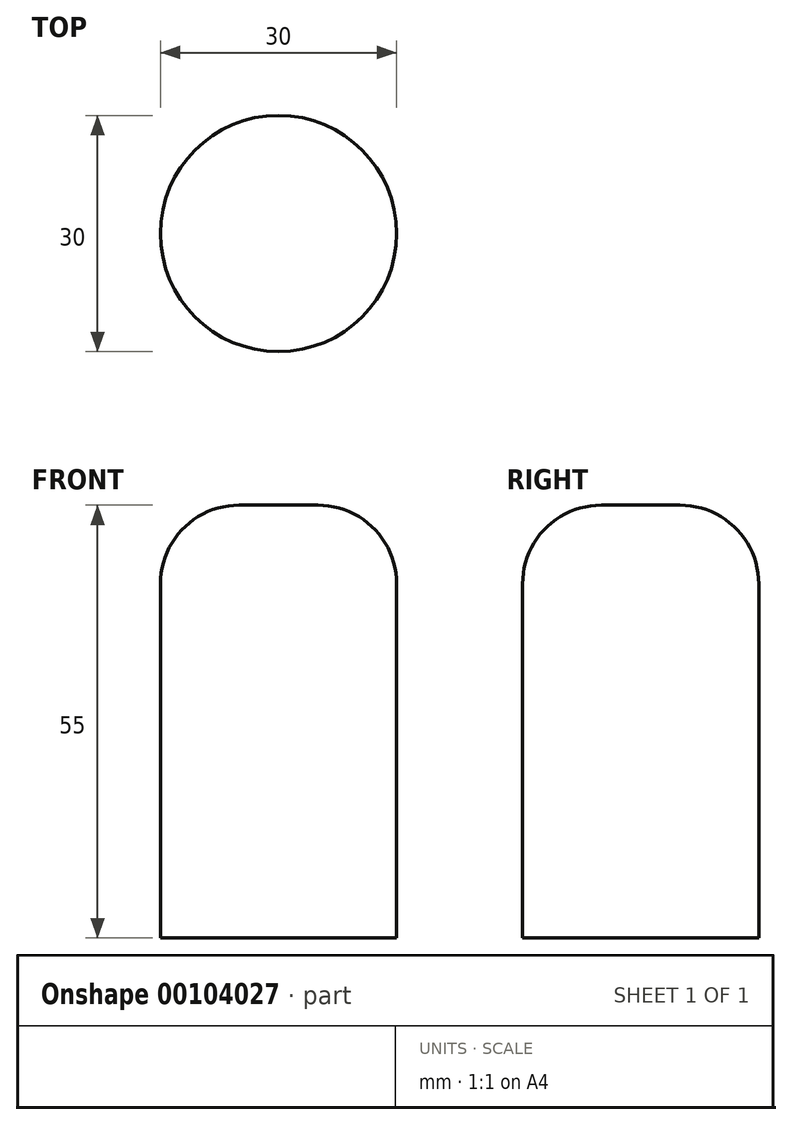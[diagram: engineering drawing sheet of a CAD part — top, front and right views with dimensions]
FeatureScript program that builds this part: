
annotation { "Feature Type Name" : "Feature", "Feature Type Description" : "" }
export const myFeature = defineFeature(function(context is Context, id is Id, definition is map)
    precondition{}
    {
        {
            var Q0;
            Q0=qCreatedBy(makeId("Top.planeOp"),FACE);
            var sketch = newSketch(context, id + "F0", { "sketchPlane" : qUnion([Q0])});
            skCircle(sketch, "E0", {"center": v(0, 0) * mm, "radius": 15 * mm});
            skSolve(sketch);
        }
        {
            var Q0;
            Q0 = qSketchRegion(id + "F0", true);
            extrude(context, id + "F1", {"entities" : qUnion([Q0]), "depth" : 55 * mm, "offsetDistance" : 25 * mm});
        }
        {
            var Q0;
            Q0=makeQuery(id+"F1.opExtrude","CAP_EDGE",EDGE,{"disambiguationData":[OSD([sQuery(id+"F0.wireOp",EDGE,"E0")])],"isStart":false});
            fillet(context, id + "F2", {"entities" : qUnion([Q0]), "tangentPropagation" : true, "radius" : 10 * mm, "defaultsChanged" : true, "vertexSettings" : [], "allowEdgeOverflow" : false});
        }
    });
